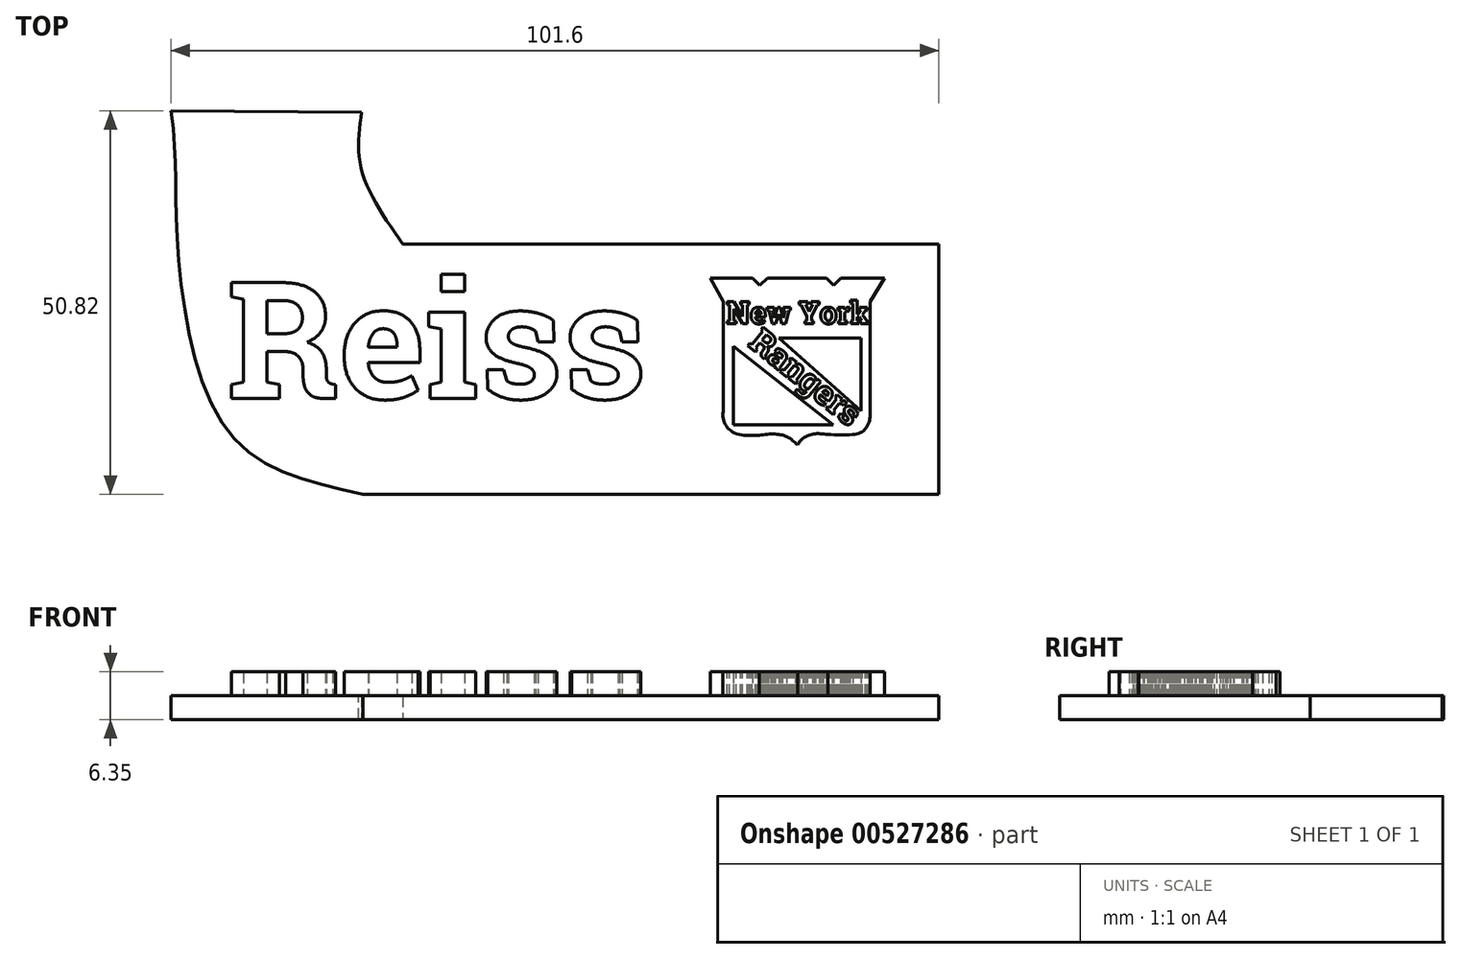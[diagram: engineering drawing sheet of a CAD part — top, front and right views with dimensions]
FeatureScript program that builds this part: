
annotation { "Feature Type Name" : "Feature", "Feature Type Description" : "" }
export const myFeature = defineFeature(function(context is Context, id is Id, definition is map)
    precondition{}
    {
        {
            var Q0;
            Q0=qCreatedBy(makeId("Top.planeOp"),FACE);
            var sketch = newSketch(context, id + "F0", { "sketchPlane" : qUnion([Q0])});
            skLineSegment(sketch, "E0.top", {"start": v(38.1, -12.7) * mm, "end": v(-38.1, -12.7) * mm});
            skLineSegment(sketch, "E0.left", {"start": v(38.1, 12.7) * mm, "end": v(38.1, -12.7) * mm});
            skPoint(sketch, "E0.middle", {"position": v(0, 0) * mm});
            skFitSpline(sketch, "E1", {"points": [v(-38.1, -12.7) * mm, v(-55.9, -4.42) * mm, v(-62.7, 21.92) * mm, v(-63.5, 38.12) * mm], "startDerivative": vector(-64.79, 14.53) * mm, "endDerivative": vector(-7.92, 55.85) * mm});
            skLineSegment(sketch, "E2", {"start": v(-63.5, 38.12) * mm, "end": v(-45.88, 37.98) * mm});
            skLineSegment(sketch, "E3", {"start": v(38.1, 12.7) * mm, "end": v(38.1, 20.44) * mm});
            skLineSegment(sketch, "E4", {"start": v(-45.88, 37.98) * mm, "end": v(-38.27, 37.91) * mm});
            skLineSegment(sketch, "E5", {"start": v(38.1, 20.44) * mm, "end": v(-32.8, 20.44) * mm});
            skFitSpline(sketch, "E6", {"points": [v(-38.27, 37.91) * mm, v(-38.27, 30.22) * mm, v(-32.8, 20.44) * mm], "startDerivative": vector(-2.26, -16.77) * mm, "endDerivative": vector(12.72, -18.14) * mm});
            skSolve(sketch);
        }
        {
            var Q0;
            Q0=makeQuery(id+"F0.imprint","IMPRINT",FACE,{"disambiguationData":[TD([[makeQuery(id+"F0.imprint","IMPRINT",EDGE,{"derivedFrom":sQuery(id+"F0.wireOp",EDGE,"E0.top")}),-1.0]])]});
            extrude(context, id + "F1", {"entities" : qUnion([Q0]), "depth" : 3.17 * mm, "offsetDistance" : 25.4 * mm});
        }
        {
            var Q0;
            Q0=makeQuery(id+"F1.opExtrude","CAP_FACE",FACE,{"disambiguationData":[OSD([sQuery(id+"F0.wireOp",EDGE,"E0.top"),sQuery(id+"F0.wireOp",EDGE,"E0.left"),sQuery(id+"F0.wireOp",EDGE,"E1"),sQuery(id+"F0.wireOp",EDGE,"E2"),sQuery(id+"F0.wireOp",EDGE,"E3"),sQuery(id+"F0.wireOp",EDGE,"E4"),sQuery(id+"F0.wireOp",EDGE,"E5"),sQuery(id+"F0.wireOp",EDGE,"E6")])],"isStart":false});
            var sketch = newSketch(context, id + "F2", { "sketchPlane" : qUnion([Q0])});
            skText(sketch, "E7", { "text": "Reiss", "fontName": "RobotoSlab-Bold.ttf"});
            const initialGuessF2  = {"E7": [-0.05612, 0, 1, 0, 0.01554]};
            skSetInitialGuess(sketch, initialGuessF2);
            skSolve(sketch);
        }
        {
            var Q0;
            Q0 = qSketchRegion(id + "F2", true);
            extrude(context, id + "F3", {"entities" : qUnion([Q0]), "operationType" : NewBodyOperationType.ADD, "depth" : 3.17 * mm, "offsetDistance" : 25.4 * mm});
        }
        {
            var Q0;
            {var subQ0=sQuery(id+"F0.wireOp",EDGE,"E3");var subQ1=sQuery(id+"F0.wireOp",EDGE,"E0.left");var subQ2=sQuery(id+"F0.wireOp",EDGE,"E4");var subQ3=sQuery(id+"F0.wireOp",EDGE,"E2");var subQ4=sQuery(id+"F0.wireOp",EDGE,"E0.top");var subQ5=sQuery(id+"F0.wireOp",EDGE,"E5");var subQ6=sQuery(id+"F0.wireOp",EDGE,"E6");var subQ7=sQuery(id+"F0.wireOp",EDGE,"E1");Q0=makeQuery(id+"F3.boolean.opBoolean","SPLIT",FACE,{"disambiguationData":[TD([makeQuery(id+"F1.opExtrude","SWEPT_FACE",FACE,{"disambiguationData":[OSD([subQ4])]})])],"derivedFrom":makeQuery(id+"F1.opExtrude","CAP_FACE",FACE,{"disambiguationData":[OSD([subQ4,subQ1,subQ7,subQ3,subQ0,subQ2,subQ5,subQ6])],"isStart":false})});}
            var sketch = newSketch(context, id + "F4", { "sketchPlane" : qUnion([Q0])});
            skLineSegment(sketch, "E8", {"start": v(7.9, 15.95) * mm, "end": v(9.6, 12.84) * mm});
            skLineSegment(sketch, "E9", {"start": v(9.6, 12.84) * mm, "end": v(9.6, -1.1) * mm});
            skFitSpline(sketch, "E10", {"points": [v(9.6, -1.1) * mm, v(9.6, -2.83) * mm, v(10.32, -4.05) * mm, v(11.64, -4.76) * mm, v(14.34, -4.86) * mm], "startDerivative": vector(-0.76, -7.37) * mm, "endDerivative": vector(9.59, 0.35) * mm});
            skFitSpline(sketch, "E11", {"points": [v(14.34, -4.86) * mm, v(17.44, -4.86) * mm, v(19.4, -6.17) * mm], "startDerivative": vector(6.28, 0.82) * mm, "endDerivative": vector(3.54, -3.79) * mm});
            skFitSpline(sketch, "E12", {"points": [v(19.4, -6.17) * mm, v(19.78, -5.57) * mm, v(21.2, -4.76) * mm, v(23.4, -4.76) * mm], "startDerivative": vector(1.56, 2.82) * mm, "endDerivative": vector(5.68, -0.63) * mm});
            skFitSpline(sketch, "E13", {"points": [v(23.4, -4.76) * mm, v(26.85, -4.76) * mm, v(28.23, -4.2) * mm, v(28.94, -2.88) * mm, v(29, -1.96) * mm], "startDerivative": vector(10.84, -0.48) * mm, "endDerivative": vector(-0.25, 4.7) * mm});
            skLineSegment(sketch, "E14", {"start": v(29, -2.25) * mm, "end": v(29, 12.84) * mm});
            skLineSegment(sketch, "E15", {"start": v(29, 12.84) * mm, "end": v(30.92, 15.95) * mm});
            skLineSegment(sketch, "E16", {"start": v(30.92, 15.95) * mm, "end": v(25.15, 15.95) * mm});
            skLineSegment(sketch, "E17", {"start": v(25.15, 15.95) * mm, "end": v(24.16, 14.98) * mm});
            skLineSegment(sketch, "E18", {"start": v(24.16, 14.98) * mm, "end": v(23.2, 15.95) * mm});
            skLineSegment(sketch, "E19", {"start": v(23.2, 15.95) * mm, "end": v(15.44, 15.95) * mm});
            skLineSegment(sketch, "E20", {"start": v(15.44, 15.95) * mm, "end": v(14.39, 14.98) * mm});
            skLineSegment(sketch, "E21", {"start": v(14.39, 14.98) * mm, "end": v(13.49, 15.95) * mm});
            skLineSegment(sketch, "E22", {"start": v(13.49, 15.95) * mm, "end": v(7.9, 15.95) * mm});
            skLineSegment(sketch, "E23", {"start": v(29, -2.25) * mm, "end": v(29, -2.26) * mm});
            skLineSegment(sketch, "E24", {"start": v(10.94, 6.92) * mm, "end": v(24.11, -3.52) * mm});
            skLineSegment(sketch, "E25", {"start": v(24.11, -3.52) * mm, "end": v(10.94, -3.52) * mm});
            skLineSegment(sketch, "E26", {"start": v(10.94, -3.52) * mm, "end": v(10.94, 6.92) * mm});
            skLineSegment(sketch, "E27", {"start": v(16.93, 8.03) * mm, "end": v(27.8, 8.03) * mm});
            skLineSegment(sketch, "E28", {"start": v(27.8, 8.03) * mm, "end": v(27.8, -1.64) * mm});
            skLineSegment(sketch, "E29", {"start": v(27.8, -1.64) * mm, "end": v(16.93, 8.03) * mm});
            skSolve(sketch);
        }
        {
            var Q0;
            Q0=makeQuery(id+"F4.imprint","IMPRINT",FACE,{"disambiguationData":[TD([[makeQuery(id+"F4.imprint","IMPRINT",EDGE,{"derivedFrom":sQuery(id+"F4.wireOp",EDGE,"E8")}),1.0]])]});
            extrude(context, id + "F5", {"entities" : qUnion([Q0]), "operationType" : NewBodyOperationType.ADD, "depth" : 3.17 * mm, "offsetDistance" : 25.4 * mm});
        }
        {
            var Q0;
            Q0=makeQuery(id+"F5.opExtrude","CAP_FACE",FACE,{"disambiguationData":[OSD([sQuery(id+"F4.wireOp",EDGE,"E8"),sQuery(id+"F4.wireOp",EDGE,"E9"),sQuery(id+"F4.wireOp",EDGE,"E10"),sQuery(id+"F4.wireOp",EDGE,"E11"),sQuery(id+"F4.wireOp",EDGE,"E12"),sQuery(id+"F4.wireOp",EDGE,"E13"),sQuery(id+"F4.wireOp",EDGE,"E14"),sQuery(id+"F4.wireOp",EDGE,"E15"),sQuery(id+"F4.wireOp",EDGE,"E16"),sQuery(id+"F4.wireOp",EDGE,"E17"),sQuery(id+"F4.wireOp",EDGE,"E18"),sQuery(id+"F4.wireOp",EDGE,"E19"),sQuery(id+"F4.wireOp",EDGE,"E20"),sQuery(id+"F4.wireOp",EDGE,"E21"),sQuery(id+"F4.wireOp",EDGE,"E22"),sQuery(id+"F4.wireOp",EDGE,"E23"),sQuery(id+"F4.wireOp",EDGE,"E24"),sQuery(id+"F4.wireOp",EDGE,"E25"),sQuery(id+"F4.wireOp",EDGE,"E26"),sQuery(id+"F4.wireOp",EDGE,"E27"),sQuery(id+"F4.wireOp",EDGE,"E28"),sQuery(id+"F4.wireOp",EDGE,"E29")])],"isStart":false});
            var sketch = newSketch(context, id + "F6", { "sketchPlane" : qUnion([Q0])});
            skText(sketch, "E30", { "text": "New York", "fontName": "RobotoSlab-Bold.ttf"});
            const initialGuessF6  = {"E30": [0.00996, 0.0099, 1, 0, 0.00294]};
            skSetInitialGuess(sketch, initialGuessF6);
            skSolve(sketch);
        }
        {
            var Q0;
            Q0 = qSketchRegion(id + "F6", true);
            extrude(context, id + "F7", {"entities" : qUnion([Q0]), "operationType" : NewBodyOperationType.REMOVE, "oppositeDirection" : true, "depth" : 3.17 * mm, "offsetDistance" : 25.4 * mm});
        }
        {
            var Q0;
            Q0=makeQuery(id+"F6.imprint","IMPRINT",FACE,{"disambiguationData":[TD([[makeQuery(id+"F6.imprint","IMPRINT",EDGE,{"derivedFrom":sQuery(id+"F6.wireOp",EDGE,"E30.sketch_text.stroke-0")}),1.0]])]});
            var sketch = newSketch(context, id + "F8", { "sketchPlane" : qUnion([Q0])});
            skText(sketch, "E31", { "text": "Rangers", "fontName": "RobotoSlab-Bold.ttf"});
            const initialGuessF8  = {"E31": [0.01275, 0.00709, 0.7769, -0.62961, 0.0032]};
            skSetInitialGuess(sketch, initialGuessF8);
            skSolve(sketch);
        }
        {
            var Q0;
            Q0 = qSketchRegion(id + "F8", true);
            extrude(context, id + "F9", {"entities" : qUnion([Q0]), "operationType" : NewBodyOperationType.REMOVE, "oppositeDirection" : true, "depth" : 3.17 * mm, "offsetDistance" : 25.4 * mm});
        }
    });
